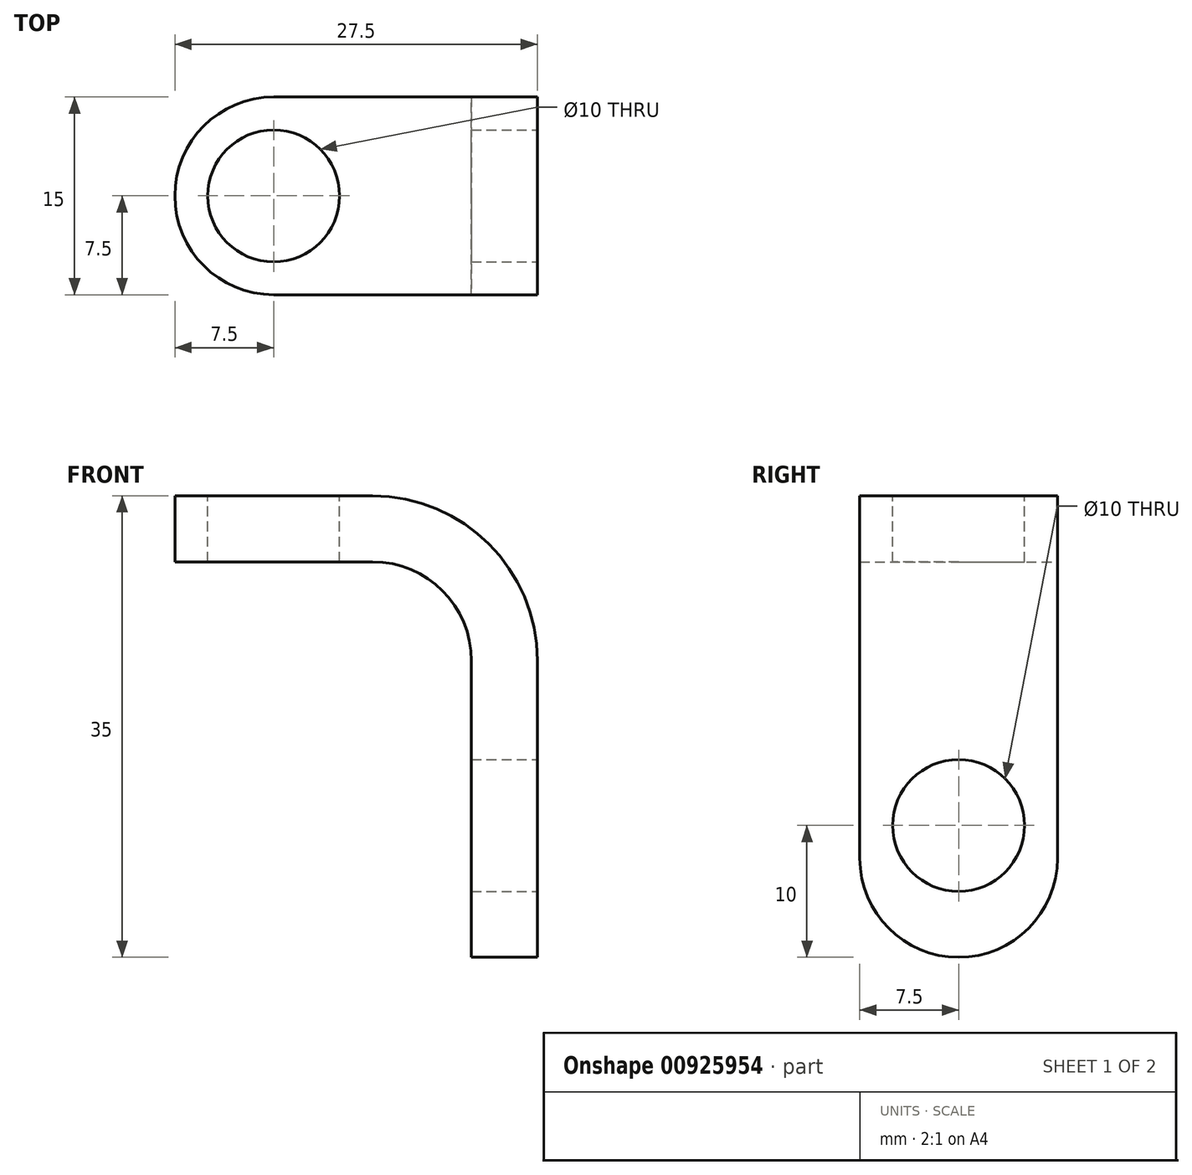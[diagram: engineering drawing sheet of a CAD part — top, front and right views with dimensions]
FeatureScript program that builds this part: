
annotation { "Feature Type Name" : "Feature", "Feature Type Description" : "" }
export const myFeature = defineFeature(function(context is Context, id is Id, definition is map)
    precondition{}
    {
        {
            var Q0;
            Q0=qCreatedBy(makeId("Front.planeOp"),FACE);
            var sketch = newSketch(context, id + "F0", { "sketchPlane" : qUnion([Q0])});
            skCircle(sketch, "E0", {"center": v(0, 0) * mm, "radius": 25 * mm, "construction": true});
            skLineSegment(sketch, "E1", {"start": v(-7.5, 25) * mm, "end": v(7.5, 25) * mm});
            skLineSegment(sketch, "E2", {"start": v(20, -10) * mm, "end": v(20, 12.5) * mm});
            skLineSegment(sketch, "E3", {"start": v(15, -10) * mm, "end": v(15, 12.5) * mm});
            skLineSegment(sketch, "E4", {"start": v(7.5, 20) * mm, "end": v(-7.5, 20) * mm});
            skLineSegment(sketch, "E5", {"start": v(-7.5, 20) * mm, "end": v(-7.5, 25) * mm});
            skLineSegment(sketch, "E6", {"start": v(15, -10) * mm, "end": v(20, -10) * mm});
            skPoint(sketch, "E7.visualSharp", {"position": v(15, 20) * mm});
            skArc(sketch, "E7.filletArc", {"start": v(15, 12.5) * mm, "mid": v(12.8, 17.8) * mm, "end": v(7.5, 20) * mm});
            skPoint(sketch, "E8.visualSharp", {"position": v(20, 25) * mm});
            skArc(sketch, "E8.filletArc", {"start": v(20, 12.5) * mm, "mid": v(16.34, 21.34) * mm, "end": v(7.5, 25) * mm});
            skSolve(sketch);
        }
        {
            var Q0;
            Q0 = qSketchRegion(id + "F0", true);
            extrude(context, id + "F1", {"entities" : qUnion([Q0]), "endBound" : BoundingType.SYMMETRIC, "depth" : 15 * mm, "offsetDistance" : 25 * mm});
        }
        {
            var Q0;
            Q0=makeQuery(id+"F1.opExtrude","CAP_EDGE",EDGE,{"disambiguationData":[OSD([sQuery(id+"F0.wireOp",EDGE,"E5")])],"isStart":false});
            var Q1;
            Q1=makeQuery(id+"F1.opExtrude","CAP_EDGE",EDGE,{"disambiguationData":[OSD([sQuery(id+"F0.wireOp",EDGE,"E5")])],"isStart":true});
            var Q2;
            Q2=makeQuery(id+"F1.opExtrude","CAP_EDGE",EDGE,{"disambiguationData":[OSD([sQuery(id+"F0.wireOp",EDGE,"E6")])],"isStart":false});
            var Q3;
            Q3=makeQuery(id+"F1.opExtrude","CAP_EDGE",EDGE,{"disambiguationData":[OSD([sQuery(id+"F0.wireOp",EDGE,"E6")])],"isStart":true});
            fillet(context, id + "F2", {"entities" : qUnion([Q0, Q1, Q2, Q3]), "radius" : 7.5 * mm, "tangentPropagation" : true, "allowEdgeOverflow" : false});
        }
        {
            var Q0;
            Q0=makeQuery(id+"F1.opExtrude","SWEPT_FACE",FACE,{"disambiguationData":[OSD([sQuery(id+"F0.wireOp",EDGE,"E1")])]});
            var sketch = newSketch(context, id + "F3", { "sketchPlane" : qUnion([Q0])});
            skCircle(sketch, "E9", {"center": v(0, 0) * mm, "radius": 5 * mm});
            skSolve(sketch);
        }
        {
            var Q0;
            Q0 = qSketchRegion(id + "F3", true);
            extrude(context, id + "F4", {"entities" : qUnion([Q0]), "operationType" : NewBodyOperationType.REMOVE, "endBound" : BoundingType.THROUGH_ALL, "oppositeDirection" : true, "depth" : 25 * mm, "offsetDistance" : 25 * mm});
        }
        {
            var Q0;
            Q0=makeQuery(id+"F1.opExtrude","SWEPT_FACE",FACE,{"disambiguationData":[OSD([sQuery(id+"F0.wireOp",EDGE,"E2")])]});
            var sketch = newSketch(context, id + "F5", { "sketchPlane" : qUnion([Q0])});
            skCircle(sketch, "E10", {"center": v(0, 0) * mm, "radius": 5 * mm});
            skSolve(sketch);
        }
        {
            var Q0;
            Q0=makeQuery(id+"F5.imprint","IMPRINT",FACE,{"disambiguationData":[TD([[makeQuery(id+"F5.imprint","IMPRINT",EDGE,{"derivedFrom":sQuery(id+"F5.wireOp",EDGE,"E10")}),1.0]])]});
            extrude(context, id + "F6", {"entities" : qUnion([Q0]), "operationType" : NewBodyOperationType.REMOVE, "endBound" : BoundingType.THROUGH_ALL, "oppositeDirection" : true, "depth" : 25 * mm, "offsetDistance" : 25 * mm});
        }
    });
